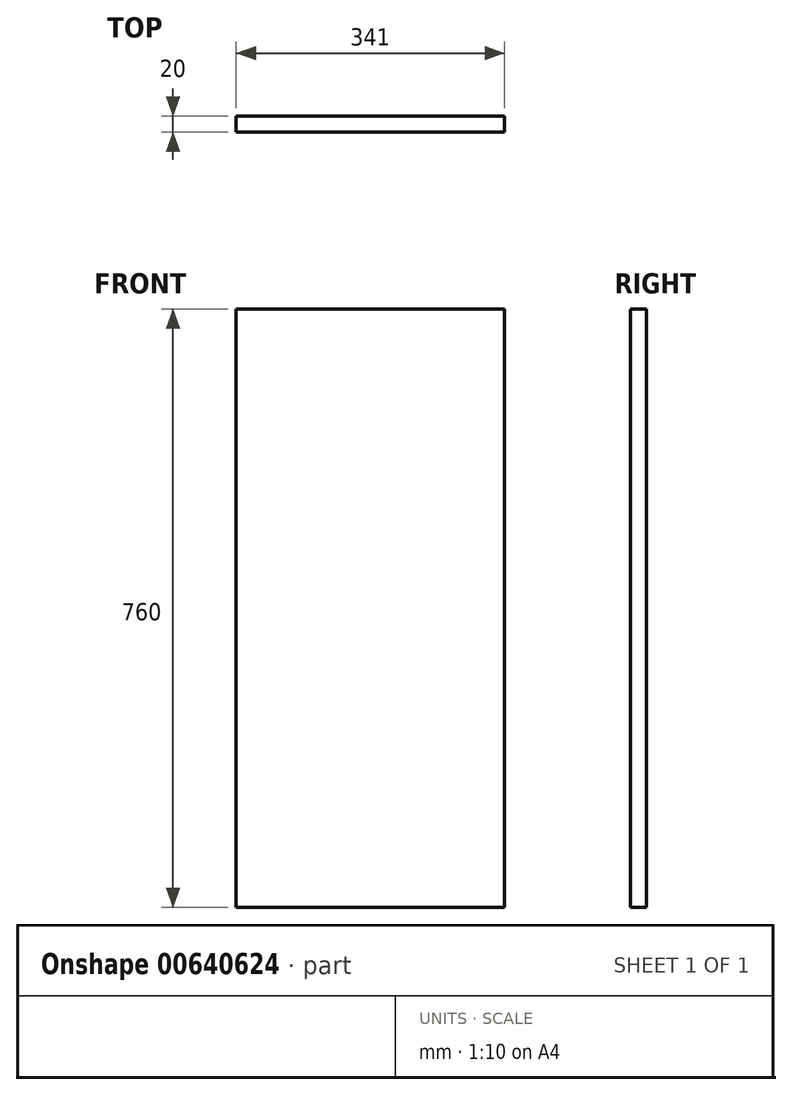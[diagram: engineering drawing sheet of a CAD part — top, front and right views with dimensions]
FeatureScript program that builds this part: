
annotation { "Feature Type Name" : "Feature", "Feature Type Description" : "" }
export const myFeature = defineFeature(function(context is Context, id is Id, definition is map)
    precondition{}
    {
        {
            var Q0;
            Q0=qCreatedBy(makeId("Front.planeOp"),FACE);
            var sketch = newSketch(context, id + "F0", { "sketchPlane" : qUnion([Q0])});
            skLineSegment(sketch, "E0.bottom", {"start": v(0, 0) * mm, "end": v(-341, 0) * mm});
            skLineSegment(sketch, "E0.top", {"start": v(0, 760) * mm, "end": v(-341, 760) * mm});
            skLineSegment(sketch, "E0.left", {"start": v(0, 0) * mm, "end": v(0, 760) * mm});
            skLineSegment(sketch, "E0.right", {"start": v(-341, 0) * mm, "end": v(-341, 760) * mm});
            skSolve(sketch);
        }
        {
            var Q0;
            Q0 = qSketchRegion(id + "F0", true);
            extrude(context, id + "F1", {"entities" : qUnion([Q0]), "depth" : 20 * mm, "offsetDistance" : 25 * mm});
        }
    });
